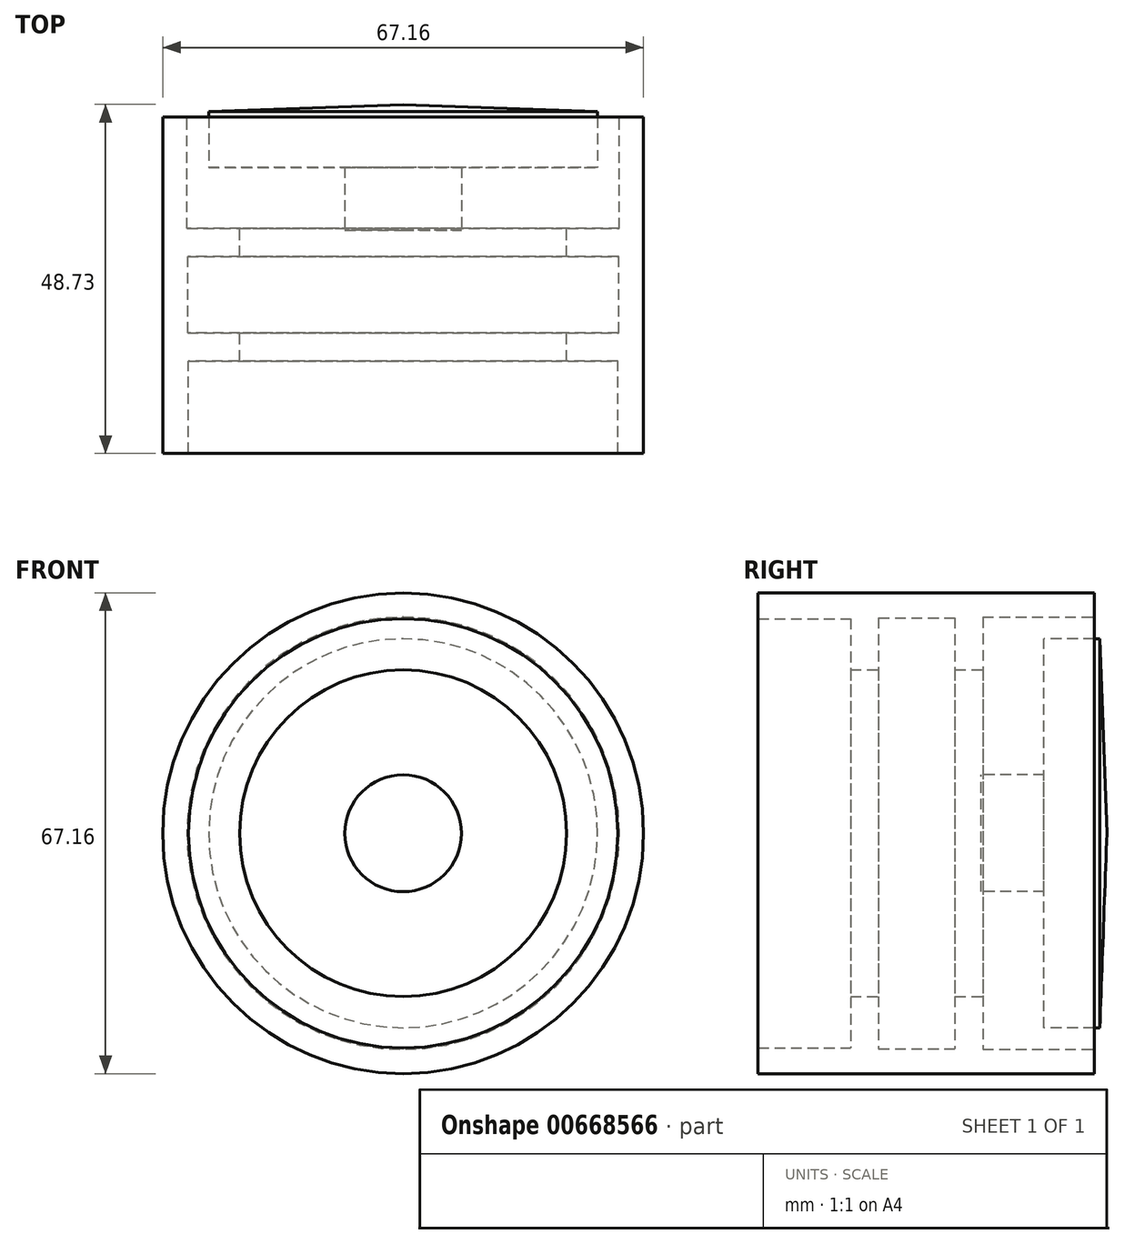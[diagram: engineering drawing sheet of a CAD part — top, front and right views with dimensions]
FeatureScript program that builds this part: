
annotation { "Feature Type Name" : "Feature", "Feature Type Description" : "" }
export const myFeature = defineFeature(function(context is Context, id is Id, definition is map)
    precondition{}
    {
        {
            var Q0;
            Q0=qCreatedBy(makeId("Right.planeOp"),FACE);
            var sketch = newSketch(context, id + "F0", { "sketchPlane" : qUnion([Q0])});
            skLineSegment(sketch, "E0", {"start": v(-7.98, 0) * mm, "end": v(-25.55, 0) * mm});
            skLineSegment(sketch, "E1", {"start": v(-25.55, 0) * mm, "end": v(-25.55, 8.16) * mm});
            skLineSegment(sketch, "E2", {"start": v(-25.55, 8.16) * mm, "end": v(-16.76, 8.16) * mm});
            skPoint(sketch, "E2.endSnap0", {"position": v(-16.76, 0) * mm});
            skLineSegment(sketch, "E3", {"start": v(-16.76, 8.16) * mm, "end": v(-16.76, 27.17) * mm});
            skLineSegment(sketch, "E4", {"start": v(-16.76, 27.17) * mm, "end": v(-8.98, 27.17) * mm});
            skLineSegment(sketch, "E5", {"start": v(-8.98, 27.17) * mm, "end": v(-7.98, 0) * mm});
            skSolve(sketch);
        }
        {
            var Q0;
            Q0=makeQuery(id+"F0.imprint","IMPRINT",FACE,{"disambiguationData":[TD([[makeQuery(id+"F0.imprint","IMPRINT",EDGE,{"derivedFrom":sQuery(id+"F0.wireOp",EDGE,"E0")}),-1.0]])]});
            var Q1;
            Q1=sQuery(id+"F0.wireOp",EDGE,"E0");
            var Q2;
            Q2=sQuery(id+"F0.wireOp",EDGE,"E0");
            revolve(context, id + "F1", {"entities" : qUnion([Q0]), "axis" : qUnion([Q1, Q2]), "revolveType" : RevolveType.FULL, "oppositeDirection" : true});
        }
        {
            var Q0;
            Q0=qCreatedBy(makeId("Right.planeOp"),FACE);
            var sketch = newSketch(context, id + "F2", { "sketchPlane" : qUnion([Q0])});
            skLineSegment(sketch, "E6", {"start": v(-9.74, 30.2) * mm, "end": v(-25.31, 30.2) * mm});
            skLineSegment(sketch, "E7", {"start": v(-25.31, 30.2) * mm, "end": v(-25.31, 22.83) * mm});
            skLineSegment(sketch, "E8", {"start": v(-25.31, 22.83) * mm, "end": v(-29.2, 22.83) * mm});
            skLineSegment(sketch, "E9", {"start": v(-29.2, 22.83) * mm, "end": v(-29.2, 30.1) * mm});
            skLineSegment(sketch, "E10", {"start": v(-29.2, 30.1) * mm, "end": v(-39.88, 30.1) * mm});
            skLineSegment(sketch, "E11", {"start": v(-39.88, 30.1) * mm, "end": v(-39.88, 22.83) * mm});
            skLineSegment(sketch, "E12", {"start": v(-39.88, 22.83) * mm, "end": v(-43.8, 22.83) * mm});
            skLineSegment(sketch, "E13", {"start": v(-43.8, 22.83) * mm, "end": v(-43.8, 29.99) * mm});
            skLineSegment(sketch, "E14", {"start": v(-43.8, 29.99) * mm, "end": v(-56.7, 29.99) * mm});
            skLineSegment(sketch, "E15", {"start": v(-56.7, 29.99) * mm, "end": v(-56.7, 33.58) * mm});
            skLineSegment(sketch, "E16", {"start": v(-56.7, 33.58) * mm, "end": v(-9.74, 33.58) * mm});
            skLineSegment(sketch, "E17", {"start": v(-9.74, 33.58) * mm, "end": v(-9.74, 30.2) * mm});
            skLineSegment(sketch, "E18", {"start": v(-19.54, 35.55) * mm, "end": v(-17.81, 30.9) * mm});
            skLineSegment(sketch, "E19", {"start": v(-27.96, 0) * mm, "end": v(-31.74, 0) * mm});
            skSolve(sketch);
        }
        {
            var Q0;
            Q0=makeQuery(id+"F2.imprint","IMPRINT",FACE,{"disambiguationData":[TD([[makeQuery(id+"F2.imprint","IMPRINT",EDGE,{"derivedFrom":sQuery(id+"F2.wireOp",EDGE,"E6")}),-1.0]])]});
            var Q1;
            Q1=sQuery(id+"F2.wireOp",EDGE,"E19");
            revolve(context, id + "F3", {"entities" : qUnion([Q0]), "axis" : qUnion([Q1]), "revolveType" : RevolveType.FULL});
        }
    });
